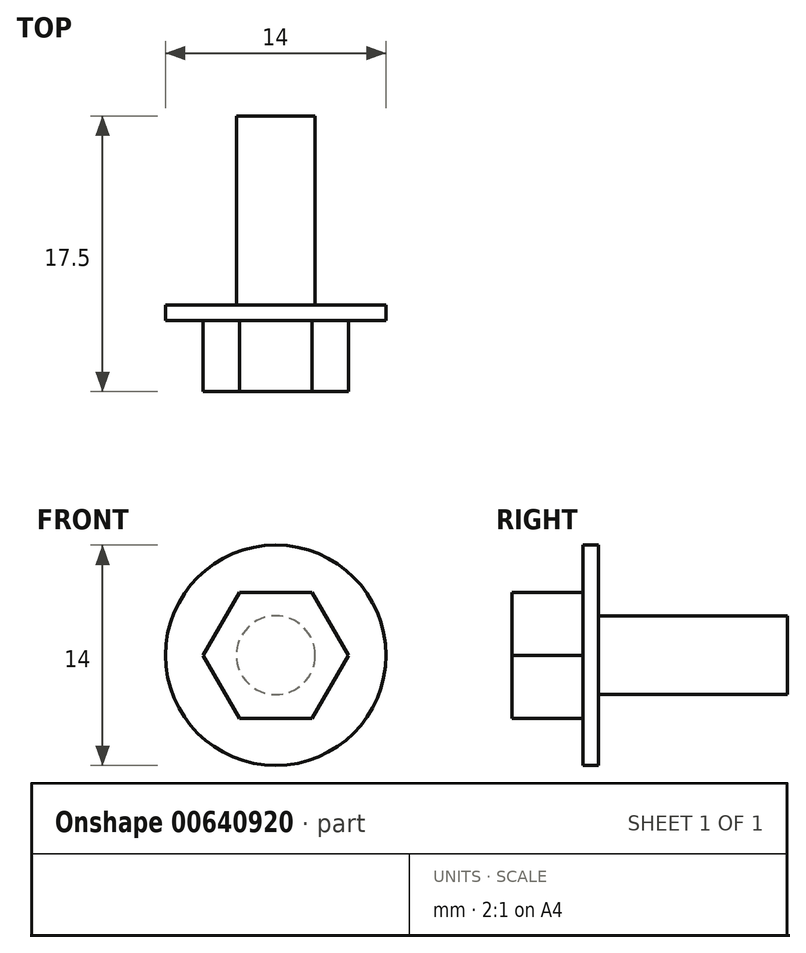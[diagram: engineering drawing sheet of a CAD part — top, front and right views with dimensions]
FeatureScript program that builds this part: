
annotation { "Feature Type Name" : "Feature", "Feature Type Description" : "" }
export const myFeature = defineFeature(function(context is Context, id is Id, definition is map)
    precondition{}
    {
        {
            var Q0;
            Q0=qCreatedBy(makeId("Front.planeOp"),FACE);
            var sketch = newSketch(context, id + "F0", { "sketchPlane" : qUnion([Q0])});
            skLineSegment(sketch, "E0", {"start": v(2.3, 0) * mm, "end": v(6.93, 0) * mm});
            skLineSegment(sketch, "E1", {"start": v(6.93, 0) * mm, "end": v(9.24, 4) * mm});
            skLineSegment(sketch, "E2", {"start": v(9.24, 4) * mm, "end": v(6.93, 8) * mm});
            skLineSegment(sketch, "E3", {"start": v(6.93, 8) * mm, "end": v(2.3, 8) * mm});
            skLineSegment(sketch, "E4", {"start": v(2.3, 8) * mm, "end": v(0, 4) * mm});
            skLineSegment(sketch, "E5", {"start": v(0, 4) * mm, "end": v(2.3, 0) * mm});
            skLineSegment(sketch, "E6", {"start": v(2.3, 8) * mm, "end": v(6.93, 0) * mm, "construction": true});
            skLineSegment(sketch, "E7", {"start": v(2.3, 0) * mm, "end": v(6.93, 8) * mm, "construction": true});
            skLineSegment(sketch, "E8", {"start": v(0, 4) * mm, "end": v(9.24, 4) * mm, "construction": true});
            skSolve(sketch);
        }
        {
            var Q0;
            Q0=qSketchRegion(id+"F0",true);
            extrude(context, id + "F1", {"entities" : qUnion([Q0]), "depth" : 5.5 * mm, "offsetDistance" : 25 * mm});
        }
        {
            var Q0;
            Q0=makeQuery(id+"F1.opExtrude","CAP_FACE",FACE,{"disambiguationData":[OSD([sQuery(id+"F0.wireOp",EDGE,"E0"),sQuery(id+"F0.wireOp",EDGE,"E1"),sQuery(id+"F0.wireOp",EDGE,"E2"),sQuery(id+"F0.wireOp",EDGE,"E3"),sQuery(id+"F0.wireOp",EDGE,"E4"),sQuery(id+"F0.wireOp",EDGE,"E5")])],"isStart":true});
            var sketch = newSketch(context, id + "F2", { "sketchPlane" : qUnion([Q0])});
            skCircle(sketch, "E9", {"center": v(-4.62, 4) * mm, "radius": 7 * mm});
            skPoint(sketch, "E9.centerSnap0", {"position": v(-4.62, 8) * mm});
            skLineSegment(sketch, "E10", {"start": v(-4.62, 4) * mm, "end": v(0, 4) * mm, "construction": true});
            skLineSegment(sketch, "E11", {"start": v(-4.62, 4) * mm, "end": v(-6.93, 0) * mm, "construction": true});
            skSolve(sketch);
        }
        {
            var Q0;
            Q0=makeQuery(id+"F2.imprint","IMPRINT",FACE,{"disambiguationData":[TD([[makeQuery(id+"F2.imprint","IMPRINT",EDGE,{"derivedFrom":sQuery(id+"F2.wireOp",EDGE,"E9")}),1.0]])]});
            extrude(context, id + "F3", {"entities" : qUnion([Q0]), "operationType" : NewBodyOperationType.ADD, "oppositeDirection" : true, "depth" : 1 * mm, "offsetDistance" : 25 * mm});
        }
        {
            var Q0;
            {var subQ0=sQuery(id+"F0.wireOp",EDGE,"E5");var subQ1=sQuery(id+"F0.wireOp",EDGE,"E4");var subQ2=sQuery(id+"F0.wireOp",EDGE,"E3");var subQ3=sQuery(id+"F0.wireOp",EDGE,"E2");var subQ4=sQuery(id+"F0.wireOp",EDGE,"E1");var subQ5=sQuery(id+"F0.wireOp",EDGE,"E0");Q0=makeQuery(id+"F3.boolean.opBoolean","MERGE",FACE,{"derivedFrom":[makeQuery(id+"F1.opExtrude","CAP_FACE",FACE,{"disambiguationData":[OSD([subQ5,subQ4,subQ3,subQ2,subQ1,subQ0])],"isStart":true}),makeQuery(id+"F3.opExtrude","CAP_FACE",FACE,{"disambiguationData":[OSD([subQ5,subQ4,subQ3,subQ2,subQ1,subQ0,sQuery(id+"F2.wireOp",EDGE,"E9")])],"isStart":true})]});}
            var sketch = newSketch(context, id + "F4", { "sketchPlane" : qUnion([Q0])});
            skCircle(sketch, "E12", {"center": v(-4.62, 4) * mm, "radius": 2.5 * mm});
            skSolve(sketch);
        }
        {
            var Q0;
            Q0=qSketchRegion(id+"F4",true);
            extrude(context, id + "F5", {"entities" : qUnion([Q0]), "operationType" : NewBodyOperationType.ADD, "depth" : 12 * mm, "offsetDistance" : 25 * mm});
        }
    });
